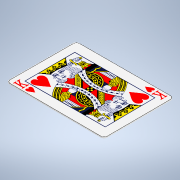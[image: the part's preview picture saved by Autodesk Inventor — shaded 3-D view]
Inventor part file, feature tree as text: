
AUTODESK INVENTOR PART (.ipt)
format: ipt  version: 2021 (Build 250183000, 183)  size: 1,414,144 bytes
history: native  units: mm
features: sketch x6, fillet x5, extrude x4, other x4, plane x2
ambient origin geometry x8: Origin, YZ Plane, XZ Plane, XY Plane, X Axis, Y Axis, Z Axis, Center Point
bodies: Solid1 (feature_tree)
feature tree (21):
  extrude  "Extrusion1"  Depth=88.9mm
  extrude  "Extrusion2"  Depth=0.8mm TaperAngle=0.0deg
  extrude  "Extrusion3"  Depth=10.0mm
  fillet  "Fillet3"  Radius=30.0mm
  fillet  "Fillet4"  Radius=30.0mm
  fillet  "Fillet5"  Radius=10.0mm
  extrude  "Extrusion5"  Depth=0.5mm
  plane  "Work Plane1"
  other  "Decal1"
  fillet  "Fillet6"  Radius=0.5mm
  fillet  "Fillet7"  Radius=0.3mm
  plane  "Work Plane2"
  other  "Decal2"
  sketch  "Sketch1"  dims[d0=63.5mm d1=88.9mm]
  sketch  "Sketch2"  dims[d2=1.0mm d3=0.0mm d6=0.8mm d7=0.0mm]
  sketch  "Sketch3"  dims[d8=10.0mm d9=10.0mm d10=30.0mm d11=30.0mm d12=10.0mm]
  sketch  "Sketch5"  dims[d13=0.6mm d14=0.0mm d15=0.5mm d16=0.5mm d17=0.3mm]
  sketch  "Sketch6"  dims[d24=87.0mm d25=0.0mm]
  other  "Image1"
  sketch  "Sketch7"  dims[d26=20.0mm d32=3.0mm d33=3.0mm d35=5.0mm]
  other  "Image2"
